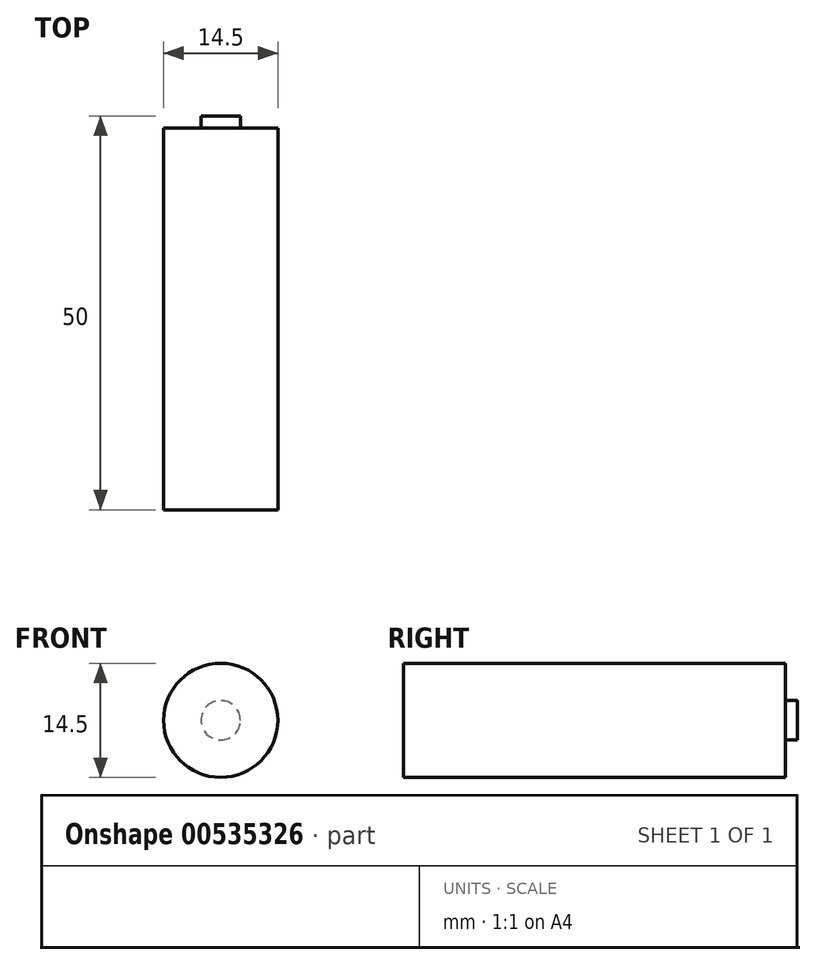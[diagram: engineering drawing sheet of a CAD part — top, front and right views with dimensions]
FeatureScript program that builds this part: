
annotation { "Feature Type Name" : "Feature", "Feature Type Description" : "" }
export const myFeature = defineFeature(function(context is Context, id is Id, definition is map)
    precondition{}
    {
        {
            var Q0;
            Q0=qCreatedBy(makeId("Front.planeOp"),FACE);
            var sketch = newSketch(context, id + "F0", { "sketchPlane" : qUnion([Q0])});
            skCircle(sketch, "E0", {"center": v(0, 0) * mm, "radius": 7.25 * mm});
            skSolve(sketch);
        }
        {
            var Q0;
            Q0=makeQuery(id+"F0.imprint","IMPRINT",FACE,{"disambiguationData":[TD([[makeQuery(id+"F0.imprint","IMPRINT",EDGE,{"derivedFrom":sQuery(id+"F0.wireOp",EDGE,"E0")}),1.0]])]});
            extrude(context, id + "F1", {"entities" : qUnion([Q0]), "depth" : 48.5 * mm, "offsetDistance" : 25 * mm});
        }
        {
            var Q0;
            Q0=makeQuery(id+"F0.imprint","IMPRINT",FACE,{"disambiguationData":[TD([[makeQuery(id+"F0.imprint","IMPRINT",EDGE,{"derivedFrom":sQuery(id+"F0.wireOp",EDGE,"E0")}),1.0]])]});
            var sketch = newSketch(context, id + "F2", { "sketchPlane" : qUnion([Q0])});
            skCircle(sketch, "E1", {"center": v(0, 0) * mm, "radius": 2.5 * mm});
            skSolve(sketch);
        }
        {
            var Q0;
            Q0=makeQuery(id+"F2.imprint","IMPRINT",FACE,{"disambiguationData":[TD([[makeQuery(id+"F2.imprint","IMPRINT",EDGE,{"derivedFrom":sQuery(id+"F2.wireOp",EDGE,"E1")}),1.0]])]});
            var Q1;
            Q1=sQuery(id+"F2.wireOp",EDGE,"E1");
            extrude(context, id + "F3", {"entities" : qUnion([Q0]), "operationType" : NewBodyOperationType.ADD, "surfaceEntities" : qUnion([Q1]), "oppositeDirection" : true, "depth" : 1.5 * mm, "offsetDistance" : 25 * mm});
        }
    });
